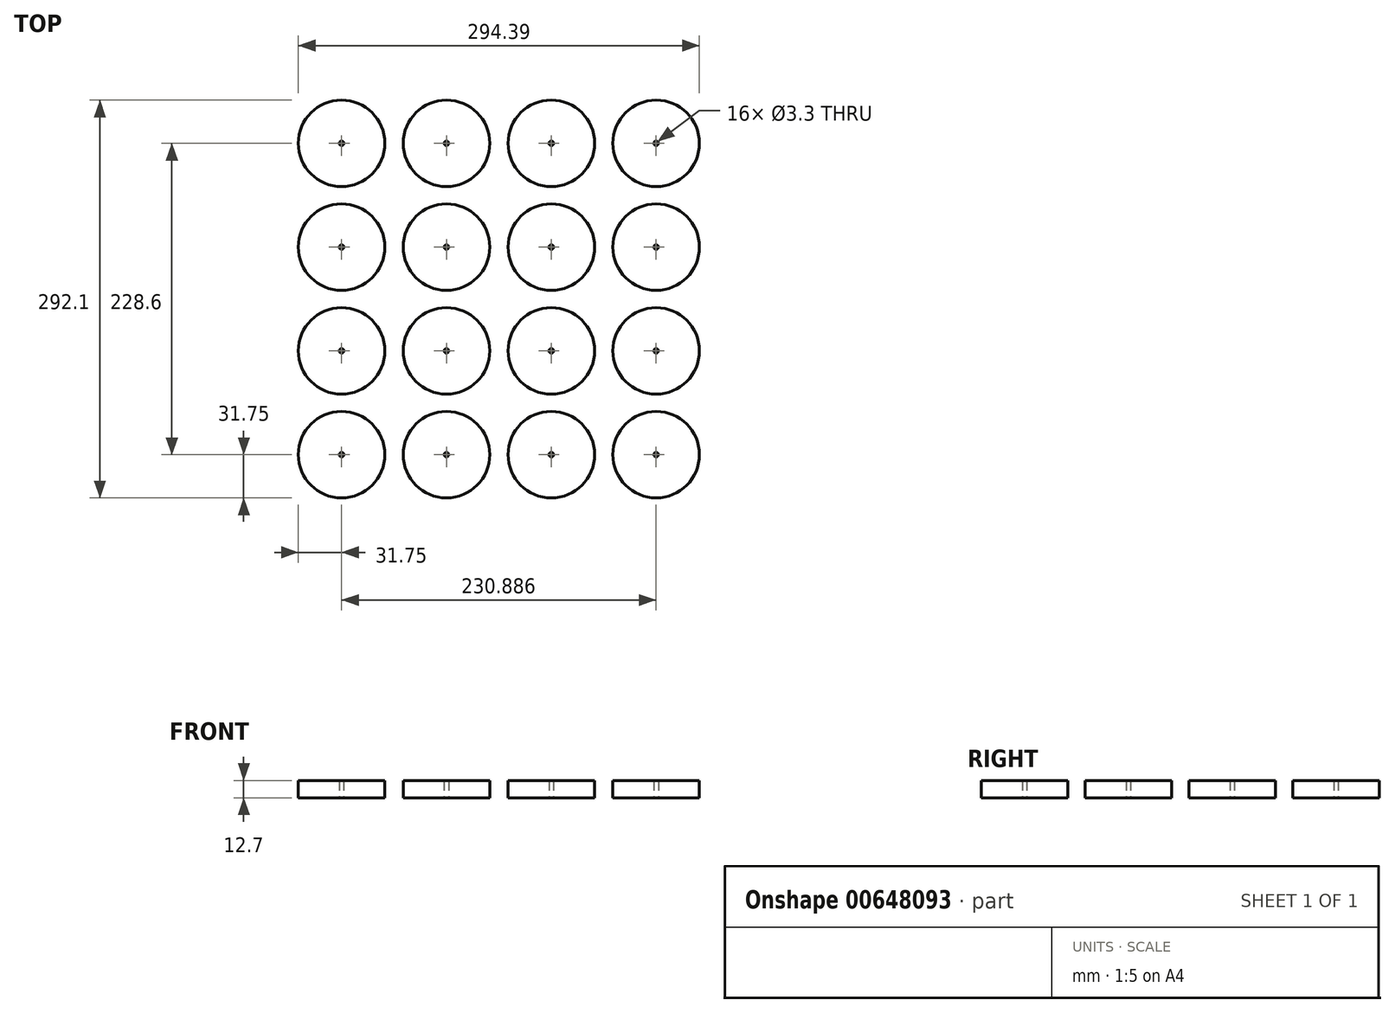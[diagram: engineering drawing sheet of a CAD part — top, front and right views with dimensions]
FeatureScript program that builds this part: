
annotation { "Feature Type Name" : "Feature", "Feature Type Description" : "" }
export const myFeature = defineFeature(function(context is Context, id is Id, definition is map)
    precondition{}
    {
        {
            var Q0;
            Q0=qCreatedBy(makeId("Top.planeOp"),FACE);
            var sketch = newSketch(context, id + "F0", { "sketchPlane" : qUnion([Q0])});
            skCircle(sketch, "E0", {"center": v(0, 0) * mm, "radius": 31.75 * mm});
            skCircle(sketch, "E1", {"center": v(0, 0) * mm, "radius": 1.65 * mm});
            skCircle(sketch, "E2.1.0.0", {"center": v(76.96, 0) * mm, "radius": 31.75 * mm});
            skCircle(sketch, "E2.1.0.1", {"center": v(76.96, 0) * mm, "radius": 1.65 * mm});
            skCircle(sketch, "E2.2.0.0", {"center": v(153.92, 0) * mm, "radius": 31.75 * mm});
            skCircle(sketch, "E2.2.0.1", {"center": v(153.92, 0) * mm, "radius": 1.65 * mm});
            skCircle(sketch, "E2.3.0.0", {"center": v(230.89, 0) * mm, "radius": 31.75 * mm});
            skCircle(sketch, "E2.3.0.1", {"center": v(230.89, 0) * mm, "radius": 1.65 * mm});
            skLineSegment(sketch, "E2.direction1", {"start": v(0, 0) * mm, "end": v(76.96, 0) * mm, "construction": true});
            skCircle(sketch, "E3.1.0.0", {"center": v(0, -76.2) * mm, "radius": 31.75 * mm});
            skCircle(sketch, "E3.1.0.1", {"center": v(153.92, -76.2) * mm, "radius": 31.75 * mm});
            skCircle(sketch, "E3.1.0.2", {"center": v(76.96, -76.2) * mm, "radius": 31.75 * mm});
            skCircle(sketch, "E3.1.0.3", {"center": v(230.89, -76.2) * mm, "radius": 31.75 * mm});
            skLineSegment(sketch, "E3.1.0.4", {"start": v(0, -76.2) * mm, "end": v(76.96, -76.2) * mm, "construction": true});
            skCircle(sketch, "E3.1.0.5", {"center": v(153.92, -76.2) * mm, "radius": 1.65 * mm});
            skCircle(sketch, "E3.1.0.6", {"center": v(230.89, -76.2) * mm, "radius": 1.65 * mm});
            skCircle(sketch, "E3.1.0.7", {"center": v(0, -76.2) * mm, "radius": 1.65 * mm});
            skCircle(sketch, "E3.1.0.8", {"center": v(76.96, -76.2) * mm, "radius": 1.65 * mm});
            skCircle(sketch, "E3.2.0.0", {"center": v(0, -152.4) * mm, "radius": 31.75 * mm});
            skCircle(sketch, "E3.2.0.1", {"center": v(153.92, -152.4) * mm, "radius": 31.75 * mm});
            skCircle(sketch, "E3.2.0.2", {"center": v(76.96, -152.4) * mm, "radius": 31.75 * mm});
            skCircle(sketch, "E3.2.0.3", {"center": v(230.89, -152.4) * mm, "radius": 31.75 * mm});
            skLineSegment(sketch, "E3.2.0.4", {"start": v(0, -152.4) * mm, "end": v(76.96, -152.4) * mm, "construction": true});
            skCircle(sketch, "E3.2.0.5", {"center": v(153.92, -152.4) * mm, "radius": 1.65 * mm});
            skCircle(sketch, "E3.2.0.6", {"center": v(230.89, -152.4) * mm, "radius": 1.65 * mm});
            skCircle(sketch, "E3.2.0.7", {"center": v(0, -152.4) * mm, "radius": 1.65 * mm});
            skCircle(sketch, "E3.2.0.8", {"center": v(76.96, -152.4) * mm, "radius": 1.65 * mm});
            skCircle(sketch, "E3.3.0.0", {"center": v(0, -228.6) * mm, "radius": 31.75 * mm});
            skCircle(sketch, "E3.3.0.1", {"center": v(153.92, -228.6) * mm, "radius": 31.75 * mm});
            skCircle(sketch, "E3.3.0.2", {"center": v(76.96, -228.6) * mm, "radius": 31.75 * mm});
            skCircle(sketch, "E3.3.0.3", {"center": v(230.89, -228.6) * mm, "radius": 31.75 * mm});
            skLineSegment(sketch, "E3.3.0.4", {"start": v(0, -228.6) * mm, "end": v(76.96, -228.6) * mm, "construction": true});
            skCircle(sketch, "E3.3.0.5", {"center": v(153.92, -228.6) * mm, "radius": 1.65 * mm});
            skCircle(sketch, "E3.3.0.6", {"center": v(230.89, -228.6) * mm, "radius": 1.65 * mm});
            skCircle(sketch, "E3.3.0.7", {"center": v(0, -228.6) * mm, "radius": 1.65 * mm});
            skCircle(sketch, "E3.3.0.8", {"center": v(76.96, -228.6) * mm, "radius": 1.65 * mm});
            skLineSegment(sketch, "E3.direction1", {"start": v(0, 0) * mm, "end": v(0, -76.2) * mm, "construction": true});
            skSolve(sketch);
        }
        {
            var Q0;
            Q0=makeQuery(id+"F0.imprint","IMPRINT",FACE,{"disambiguationData":[TD([[makeQuery(id+"F0.imprint","IMPRINT",EDGE,{"derivedFrom":sQuery(id+"F0.wireOp",EDGE,"E0")}),1.0]])]});
            var Q1;
            Q1=makeQuery(id+"F0.imprint","IMPRINT",FACE,{"disambiguationData":[TD([[makeQuery(id+"F0.imprint","IMPRINT",EDGE,{"derivedFrom":sQuery(id+"F0.wireOp",EDGE,"E2.1.0.0")}),1.0]])]});
            var Q2;
            Q2=makeQuery(id+"F0.imprint","IMPRINT",FACE,{"disambiguationData":[TD([[makeQuery(id+"F0.imprint","IMPRINT",EDGE,{"derivedFrom":sQuery(id+"F0.wireOp",EDGE,"E2.2.0.0")}),1.0]])]});
            var Q3;
            Q3=makeQuery(id+"F0.imprint","IMPRINT",FACE,{"disambiguationData":[TD([[makeQuery(id+"F0.imprint","IMPRINT",EDGE,{"derivedFrom":sQuery(id+"F0.wireOp",EDGE,"E2.3.0.0")}),1.0]])]});
            var Q4;
            Q4=makeQuery(id+"F0.imprint","IMPRINT",FACE,{"disambiguationData":[TD([[makeQuery(id+"F0.imprint","IMPRINT",EDGE,{"derivedFrom":sQuery(id+"F0.wireOp",EDGE,"E3.1.0.3")}),1.0]])]});
            var Q5;
            Q5=makeQuery(id+"F0.imprint","IMPRINT",FACE,{"disambiguationData":[TD([[makeQuery(id+"F0.imprint","IMPRINT",EDGE,{"derivedFrom":sQuery(id+"F0.wireOp",EDGE,"E3.1.0.1")}),1.0]])]});
            var Q6;
            Q6=makeQuery(id+"F0.imprint","IMPRINT",FACE,{"disambiguationData":[TD([[makeQuery(id+"F0.imprint","IMPRINT",EDGE,{"derivedFrom":sQuery(id+"F0.wireOp",EDGE,"E3.1.0.2")}),1.0]])]});
            var Q7;
            Q7=makeQuery(id+"F0.imprint","IMPRINT",FACE,{"disambiguationData":[TD([[makeQuery(id+"F0.imprint","IMPRINT",EDGE,{"derivedFrom":sQuery(id+"F0.wireOp",EDGE,"E3.1.0.0")}),1.0]])]});
            var Q8;
            Q8=makeQuery(id+"F0.imprint","IMPRINT",FACE,{"disambiguationData":[TD([[makeQuery(id+"F0.imprint","IMPRINT",EDGE,{"derivedFrom":sQuery(id+"F0.wireOp",EDGE,"E3.2.0.0")}),1.0]])]});
            var Q9;
            Q9=makeQuery(id+"F0.imprint","IMPRINT",FACE,{"disambiguationData":[TD([[makeQuery(id+"F0.imprint","IMPRINT",EDGE,{"derivedFrom":sQuery(id+"F0.wireOp",EDGE,"E3.2.0.2")}),1.0]])]});
            var Q10;
            Q10=makeQuery(id+"F0.imprint","IMPRINT",FACE,{"disambiguationData":[TD([[makeQuery(id+"F0.imprint","IMPRINT",EDGE,{"derivedFrom":sQuery(id+"F0.wireOp",EDGE,"E3.2.0.1")}),1.0]])]});
            var Q11;
            Q11=makeQuery(id+"F0.imprint","IMPRINT",FACE,{"disambiguationData":[TD([[makeQuery(id+"F0.imprint","IMPRINT",EDGE,{"derivedFrom":sQuery(id+"F0.wireOp",EDGE,"E3.2.0.3")}),1.0]])]});
            var Q12;
            Q12=makeQuery(id+"F0.imprint","IMPRINT",FACE,{"disambiguationData":[TD([[makeQuery(id+"F0.imprint","IMPRINT",EDGE,{"derivedFrom":sQuery(id+"F0.wireOp",EDGE,"E3.3.0.3")}),1.0]])]});
            var Q13;
            Q13=makeQuery(id+"F0.imprint","IMPRINT",FACE,{"disambiguationData":[TD([[makeQuery(id+"F0.imprint","IMPRINT",EDGE,{"derivedFrom":sQuery(id+"F0.wireOp",EDGE,"E3.3.0.1")}),1.0]])]});
            var Q14;
            Q14=makeQuery(id+"F0.imprint","IMPRINT",FACE,{"disambiguationData":[TD([[makeQuery(id+"F0.imprint","IMPRINT",EDGE,{"derivedFrom":sQuery(id+"F0.wireOp",EDGE,"E3.3.0.2")}),1.0]])]});
            var Q15;
            Q15=makeQuery(id+"F0.imprint","IMPRINT",FACE,{"disambiguationData":[TD([[makeQuery(id+"F0.imprint","IMPRINT",EDGE,{"derivedFrom":sQuery(id+"F0.wireOp",EDGE,"E3.3.0.0")}),1.0]])]});
            extrude(context, id + "F1", {"entities" : qUnion([Q0, Q1, Q2, Q3, Q4, Q5, Q6, Q7, Q8, Q9, Q10, Q11, Q12, Q13, Q14, Q15]), "depth" : 12.7 * mm, "offsetDistance" : 25.4 * mm});
        }
    });
